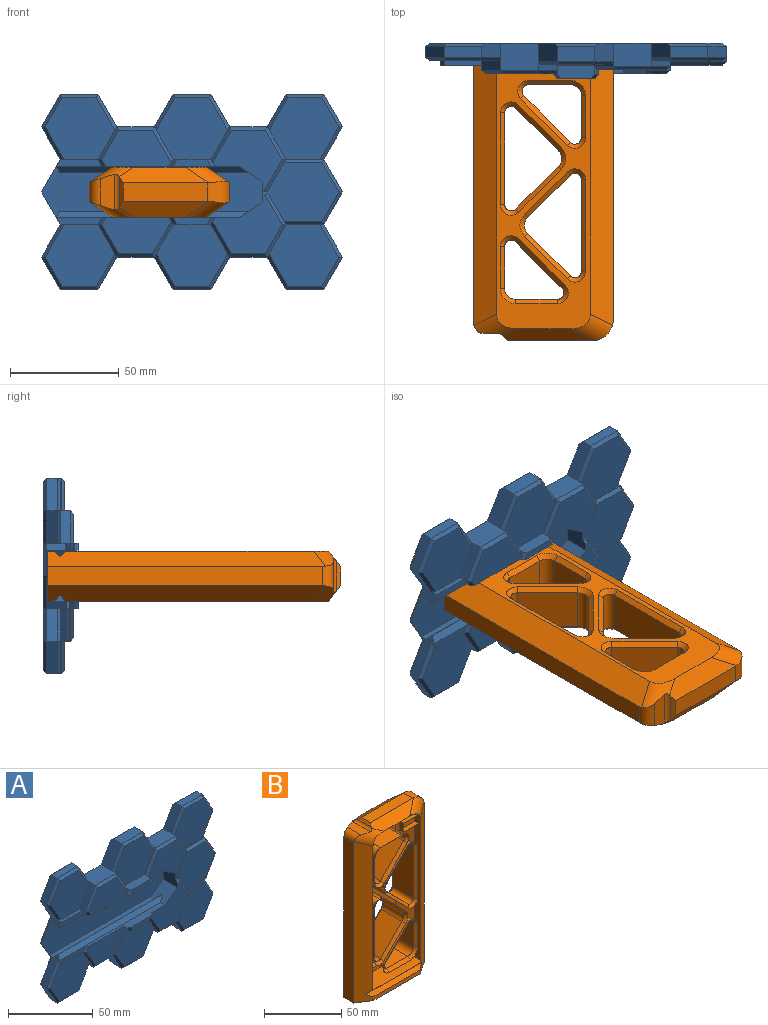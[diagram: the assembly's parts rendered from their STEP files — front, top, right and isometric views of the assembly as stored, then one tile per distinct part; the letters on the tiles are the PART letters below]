
ASSEMBLY  parts=2 mates=1
PART A: 150 faces, bbox 138.6x16x90 mm
  f0: plane 135.1x87mm, normal (0,1,0), area 9642.8mm2, adj f32,f33,f34,f36,f38,f39,f40,f42
  f1: plane 88.32x2.61mm, normal (0,0.71,0.71), area 315.8mm2, adj f2,f4,f65,f149
  f2: plane 88.32x2.61mm, normal (0,-0.71,0.71), area 315.8mm2, adj f1,f65,f66,f77,f149
  f3: plane 101.93x23.5mm, normal (0,-1,0), area 2228.6mm2, adj f4,f5,f6,f8,f9,f17,f30,f65
  f4: plane 84.4x3.14mm, normal (0,0,1), area 265.1mm2, adj f1,f3,f9,f65
  f5: plane 84.4x3.14mm, normal (0,0,-1), area 265.1mm2, adj f3,f8,f17,f147
  f6: plane 12.1x9.2mm, normal (-1,0,0), area 101mm2, adj f3,f8,f10,f12,f65,f70,f145
  f7: plane 63.32x5.74mm, normal (0,0,-1), area 252.4mm2, adj f8,f12,f64,f68,f69,f72,f73,f80
  f8: plane 10.75x10.1mm, normal (-0.55,0,-0.83), area 118.1mm2, adj f3,f5,f6,f7,f12,f80,f147
  f9: plane 15x8.76mm, normal (-0.87,0,-0.5), area 38.3mm2, adj f3,f4,f17,f18,f76,f77,f139,f149
  f10: plane 32.04x27mm, normal (0,-1,0), area 495.5mm2, adj f6,f65,f66,f75,f110,f111,f112,f113
  f11: plane 32.04x16.75mm, normal (0,-1,0), area 415.2mm2, adj f66,f71,f86,f87,f88,f89
  f12: plane 32.04x28.5mm, normal (0,-1,0), area 496.6mm2, adj f6,f7,f8,f69,f70,f82,f83,f84
  f13: plane 17.32x7mm, normal (0,0,1), area 121.2mm2, adj f33,f34,f100,f138
  f14: plane 17.32x5mm, normal (0,0,1), area 86.6mm2, adj f15,f36,f95,f143
  f15: plane 15x8.66mm, normal (-0.87,0,0.5), area 86.6mm2, adj f14,f16,f96,f142
  f16: plane 15x8.66mm, normal (-0.87,0,-0.5), area 86.6mm2, adj f15,f17,f97,f141
  f17: plane 15x8.76mm, normal (-0.87,0,0.5), area 38.3mm2, adj f3,f5,f9,f16,f78,f79,f140,f148
  f18: plane 15x8.66mm, normal (-0.87,0,0.5), area 86.6mm2, adj f9,f19,f137,f146
  f19: plane 15x8.66mm, normal (-0.87,0,-0.5), area 86.6mm2, adj f18,f20,f123,f136
  f20: plane 17.32x5mm, normal (0,0,-1), area 86.6mm2, adj f19,f42,f124,f135
  f21: plane 17.32x7mm, normal (0,0,-1), area 121.2mm2, adj f39,f40,f121,f131
  f22: plane 17.32x5mm, normal (0,0,-1), area 86.6mm2, adj f23,f38,f117,f126
  f23: plane 15x8.66mm, normal (0.87,0,-0.5), area 86.6mm2, adj f22,f24,f118,f127
  f24: plane 15x8.66mm, normal (0.87,0,0.5), area 86.6mm2, adj f23,f25,f119,f128
  f25: plane 15x8.66mm, normal (0.87,0,-0.5), area 121.2mm2, adj f24,f26,f45,f107,f129
  f26: plane 15x8.66mm, normal (0.87,0,0.5), area 121.2mm2, adj f25,f27,f44,f108,f130
  f27: plane 15x8.66mm, normal (0.87,0,-0.5), area 86.6mm2, adj f26,f28,f102,f132
  f28: plane 15x8.66mm, normal (0.87,0,0.5), area 86.6mm2, adj f27,f29,f103,f133
  f29: plane 17.32x5mm, normal (0,0,1), area 86.6mm2, adj f28,f32,f104,f134
  f30: cylinder r=1.8mm len=3.6mm, axis (0,1,0), area 10.2mm2, adj f3,f81
  f31: plane 32.04x28.5mm, normal (0,-1,0), area 678.1mm2, adj f44,f56,f102,f103,f104,f105
  f32: plane 15x8.66mm, normal (-0.87,0,0.5), area 111.3mm2, adj f0,f29,f62,f105,f134
  f33: plane 15x8.66mm, normal (0.87,0,0.5), area 145.9mm2, adj f0,f13,f62,f99,f138
  f34: plane 15x8.66mm, normal (-0.87,0,0.5), area 145.9mm2, adj f0,f13,f63,f101,f138
  f35: plane 32.04x28.5mm, normal (0,-1,0), area 678.1mm2, adj f51,f78,f94,f95,f96,f97
  f36: plane 15x8.66mm, normal (0.87,0,0.5), area 111.3mm2, adj f0,f14,f63,f94,f143
  f37: plane 32.04x28.5mm, normal (0,-1,0), area 678.1mm2, adj f45,f59,f116,f117,f118,f119
  f38: plane 15x8.66mm, normal (-0.87,0,-0.5), area 111.3mm2, adj f0,f22,f61,f116,f126
  f39: plane 15x8.66mm, normal (-0.87,0,-0.5), area 145.9mm2, adj f0,f21,f60,f120,f131
  f40: plane 15x8.66mm, normal (0.87,0,-0.5), area 145.9mm2, adj f0,f21,f61,f122,f131
  f41: plane 32.04x28.5mm, normal (0,-1,0), area 678.1mm2, adj f57,f76,f123,f124,f125,f146
  f42: plane 15x8.66mm, normal (0.87,0,-0.5), area 111.3mm2, adj f0,f20,f60,f125,f135
  f43: plane 32.91x28.5mm, normal (0,-1,0), area 702.8mm2, adj f48,f49,f50,f99,f100,f101
  f44: plane 17.32x2mm, normal (0,0,1), area 10mm2, adj f26,f31,f56,f102,f109
  f45: plane 17.32x2mm, normal (0,0,-1), area 10mm2, adj f25,f37,f59,f106,f119
  f46: plane 32.91x27mm, normal (0,-1,0), area 678.1mm2, adj f55,f58,f106,f107,f108,f109
  f47: plane 32.91x28.5mm, normal (0,-1,0), area 702.8mm2, adj f52,f53,f54,f120,f121,f122
  f48: plane 15x8.66mm, normal (-0.87,0,0.5), area 10mm2, adj f43,f50,f62,f85,f99
  f49: plane 15x8.66mm, normal (0.87,0,0.5), area 44.6mm2, adj f43,f50,f63,f90,f101
  f50: plane 17.32x6mm, normal (0,0,1), area 101.3mm2, adj f43,f48,f49,f69,f72,f73,f98,f144
  f51: plane 15x8.66mm, normal (-0.87,0,0.5), area 79.2mm2, adj f35,f63,f64,f78,f92,f94
  f52: plane 15x8.66mm, normal (-0.87,0,-0.5), area 44.6mm2, adj f47,f53,f61,f110,f122
  f53: plane 17.32x6mm, normal (0,0,-1), area 101.3mm2, adj f47,f52,f54,f71,f74,f75,f114,f115
  f54: plane 15x8.66mm, normal (0.87,0,-0.5), area 10mm2, adj f47,f53,f60,f86,f120
  f55: plane 15x8.66mm, normal (0.87,0,-0.5), area 10mm2, adj f46,f56,f58,f82,f109
  f56: plane 15x8.66mm, normal (0.87,0,0.5), area 44.6mm2, adj f31,f44,f55,f62,f83,f105
  f57: plane 15x8.66mm, normal (-0.87,0,-0.5), area 44.6mm2, adj f41,f60,f67,f76,f88,f125
  f58: plane 15x8.66mm, normal (0.87,0,0.5), area 44.6mm2, adj f46,f55,f59,f70,f106,f113
  f59: plane 15x8.66mm, normal (0.87,0,-0.5), area 79.2mm2, adj f37,f45,f58,f61,f112,f116
  f60: plane 17.32x10.5mm, normal (0,0,-1), area 181.9mm2, adj f0,f39,f42,f54,f57,f87
  f61: plane 17.32x12.5mm, normal (0,0,-1), area 216.5mm2, adj f0,f38,f40,f52,f59,f111
  f62: plane 17.32x10.5mm, normal (0,0,1), area 181.9mm2, adj f0,f32,f33,f48,f56,f84
  f63: plane 17.32x12.5mm, normal (0,0,1), area 216.5mm2, adj f0,f34,f36,f49,f51,f91
  f64: plane 3.25x2.24mm, normal (-0.87,0,-0.5), area 8.4mm2, adj f7,f51,f79,f93
  f65: plane 12.1x10.75mm, normal (-0.55,0,0.83), area 143.9mm2, adj f1,f2,f3,f4,f6,f10,f66
  f66: plane 63.32x5.74mm, normal (0,0,1), area 213.4mm2, adj f2,f10,f11,f65,f67,f71,f74,f75
  f67: plane 3.25x1.88mm, normal (-0.87,0,0.5), area 0.9mm2, adj f57,f66,f77,f89
  f68: plane 32.04x16.75mm, normal (0,-1,0), area 415.2mm2, adj f7,f73,f90,f91,f92,f93
  f69: plane 4x3.25mm, normal (0.87,0,0.5), area 10.7mm2, adj f7,f12,f50,f85,f144
  f70: plane 2x1.99mm, normal (0,0,1), area 2.3mm2, adj f6,f12,f58,f82,f145
  f71: plane 4x3.25mm, normal (-0.87,0,-0.5), area 10.7mm2, adj f11,f53,f66,f86,f114
  f72: plane 17.61x3.25mm, normal (0,-1,0), area 51.1mm2, adj f7,f50,f98,f144
  f73: plane 3.25x2mm, normal (-0.87,0,0.5), area 3.2mm2, adj f7,f50,f68,f90,f98
  f74: plane 17.61x3.25mm, normal (0,-1,0), area 51.1mm2, adj f53,f66,f114,f115
  f75: plane 3.25x2mm, normal (0.87,0,-0.5), area 3.2mm2, adj f10,f53,f66,f110,f115
  f76: plane 17.32x3.76mm, normal (0,0,-1), area 40.4mm2, adj f9,f41,f57,f77,f146
  f77: plane 21.07x3.25mm, normal (0,-1,0), area 62.4mm2, adj f2,f9,f67,f76
  f78: plane 17.32x3.76mm, normal (0,0,1), area 40.4mm2, adj f17,f35,f51,f79,f97
  f79: plane 21.07x3.25mm, normal (0,-1,0), area 62.4mm2, adj f17,f64,f78,f80
  f80: plane 88.32x2.61mm, normal (0,-0.71,-0.71), area 315.8mm2, adj f7,f8,f79,f147,f148
  f81: cone r=2.8mm half-angle=45deg, axis (0,1,0), area 20.4mm2, adj f0,f30
  f82: plane 15x10.39mm, normal (0.61,-0.71,-0.35), area 36.7mm2, adj f12,f55,f70,f83
  f83: plane 15x9.53mm, normal (0.61,-0.71,0.35), area 34.9mm2, adj f12,f56,f82,f84
  f84: plane 17.32x1.5mm, normal (0,-0.71,0.71), area 34.9mm2, adj f12,f62,f83,f85
  f85: plane 16.5x9.53mm, normal (-0.61,-0.71,0.35), area 36.7mm2, adj f12,f48,f69,f84
  f86: plane 16.5x9.53mm, normal (0.61,-0.71,-0.35), area 36.7mm2, adj f11,f54,f71,f87
  f87: plane 17.32x1.5mm, normal (0,-0.71,-0.71), area 34.9mm2, adj f11,f60,f86,f88
  f88: plane 15x9.53mm, normal (-0.61,-0.71,-0.35), area 34.9mm2, adj f11,f57,f87,f89
  f89: plane 3.61x3.25mm, normal (-0.61,-0.71,0.35), area 8mm2, adj f11,f66,f67,f88
  f90: plane 16.5x9.53mm, normal (0.61,-0.71,0.35), area 36.7mm2, adj f49,f68,f73,f91
  f91: plane 17.32x1.5mm, normal (0,-0.71,0.71), area 34.9mm2, adj f63,f68,f90,f92
  f92: plane 15x9.53mm, normal (-0.61,-0.71,0.35), area 34.9mm2, adj f51,f68,f91,f93
  f93: plane 3.61x3.25mm, normal (-0.61,-0.71,-0.35), area 8mm2, adj f7,f64,f68,f92
  f94: plane 16.5x9.53mm, normal (0.61,-0.71,0.35), area 36.7mm2, adj f35,f36,f51,f95
  f95: plane 17.32x1.5mm, normal (0,-0.71,0.71), area 34.9mm2, adj f14,f35,f94,f96
  f96: plane 15x9.53mm, normal (-0.61,-0.71,0.35), area 34.9mm2, adj f15,f35,f95,f97
  f97: plane 15x10.39mm, normal (-0.61,-0.71,-0.35), area 36.7mm2, adj f16,f35,f78,f96
  f98: plane 3.61x3.25mm, normal (-0.61,-0.71,0.35), area 8mm2, adj f7,f50,f72,f73
  f99: plane 16.5x9.53mm, normal (0.61,-0.71,0.35), area 36.7mm2, adj f33,f43,f48,f100
  f100: plane 17.32x1.5mm, normal (0,-0.71,0.71), area 34.9mm2, adj f13,f43,f99,f101
  f101: plane 16.5x9.53mm, normal (-0.61,-0.71,0.35), area 36.7mm2, adj f34,f43,f49,f100
  f102: plane 15x10.39mm, normal (0.61,-0.71,-0.35), area 36.7mm2, adj f27,f31,f44,f103
  f103: plane 15x9.53mm, normal (0.61,-0.71,0.35), area 34.9mm2, adj f28,f31,f102,f104
  f104: plane 17.32x1.5mm, normal (0,-0.71,0.71), area 34.9mm2, adj f29,f31,f103,f105
  f105: plane 16.5x9.53mm, normal (-0.61,-0.71,0.35), area 36.7mm2, adj f31,f32,f56,f104
  f106: plane 18.19x1.5mm, normal (0,-0.71,-0.71), area 36.7mm2, adj f45,f46,f58,f107
  f107: plane 15x9.53mm, normal (0.61,-0.71,-0.35), area 34.9mm2, adj f25,f46,f106,f108
  f108: plane 15x9.53mm, normal (0.61,-0.71,0.35), area 34.9mm2, adj f26,f46,f107,f109
  f109: plane 18.19x1.5mm, normal (0,-0.71,0.71), area 36.7mm2, adj f44,f46,f55,f108
  f110: plane 16.5x9.53mm, normal (-0.61,-0.71,-0.35), area 36.7mm2, adj f10,f52,f75,f111
  f111: plane 17.32x1.5mm, normal (0,-0.71,-0.71), area 34.9mm2, adj f10,f61,f110,f112
  f112: plane 15x9.53mm, normal (0.61,-0.71,-0.35), area 34.9mm2, adj f10,f59,f111,f113
  f113: plane 15x9.53mm, normal (0.61,-0.71,0.35), area 34.9mm2, adj f10,f58,f112,f145
  f114: plane 3.61x3.25mm, normal (-0.61,-0.71,-0.35), area 8mm2, adj f53,f66,f71,f74
  f115: plane 3.61x3.25mm, normal (0.61,-0.71,-0.35), area 8mm2, adj f53,f66,f74,f75
  f116: plane 16.5x9.53mm, normal (-0.61,-0.71,-0.35), area 36.7mm2, adj f37,f38,f59,f117
  f117: plane 17.32x1.5mm, normal (0,-0.71,-0.71), area 34.9mm2, adj f22,f37,f116,f118
  f118: plane 15x9.53mm, normal (0.61,-0.71,-0.35), area 34.9mm2, adj f23,f37,f117,f119
  f119: plane 15x10.39mm, normal (0.61,-0.71,0.35), area 36.7mm2, adj f24,f37,f45,f118
  f120: plane 16.5x9.53mm, normal (-0.61,-0.71,-0.35), area 36.7mm2, adj f39,f47,f54,f121
  f121: plane 17.32x1.5mm, normal (0,-0.71,-0.71), area 34.9mm2, adj f21,f47,f120,f122
  f122: plane 16.5x9.53mm, normal (0.61,-0.71,-0.35), area 36.7mm2, adj f40,f47,f52,f121
  f123: plane 15x9.53mm, normal (-0.61,-0.71,-0.35), area 34.9mm2, adj f19,f41,f124,f146
  f124: plane 17.32x1.5mm, normal (0,-0.71,-0.71), area 34.9mm2, adj f20,f41,f123,f125
  f125: plane 16.5x9.53mm, normal (0.61,-0.71,-0.35), area 36.7mm2, adj f41,f42,f57,f124
  f126: plane 18.19x1.5mm, normal (0,0.71,-0.71), area 36.7mm2, adj f0,f22,f38,f127
  f127: plane 15x9.53mm, normal (0.61,0.71,-0.35), area 34.9mm2, adj f0,f23,f126,f128
  f128: plane 15x10.39mm, normal (0.61,0.71,0.35), area 36.7mm2, adj f0,f24,f127,f129
  f129: plane 15x10.39mm, normal (0.61,0.71,-0.35), area 36.7mm2, adj f0,f25,f128,f130
  f130: plane 15x10.39mm, normal (0.61,0.71,0.35), area 36.7mm2, adj f0,f26,f129,f132
  f131: plane 19.05x1.5mm, normal (0,0.71,-0.71), area 38.6mm2, adj f0,f21,f39,f40
  f132: plane 15x10.39mm, normal (0.61,0.71,-0.35), area 36.7mm2, adj f0,f27,f130,f133
  f133: plane 15x9.53mm, normal (0.61,0.71,0.35), area 34.9mm2, adj f0,f28,f132,f134
  f134: plane 18.19x1.5mm, normal (0,0.71,0.71), area 36.7mm2, adj f0,f29,f32,f133
  f135: plane 18.19x1.5mm, normal (0,0.71,-0.71), area 36.7mm2, adj f0,f20,f42,f136
  f136: plane 15x9.53mm, normal (-0.61,0.71,-0.35), area 34.9mm2, adj f0,f19,f135,f137
  f137: plane 15x10.39mm, normal (-0.61,0.71,0.35), area 36.7mm2, adj f0,f18,f136,f139
  f138: plane 19.05x1.5mm, normal (0,0.71,0.71), area 38.6mm2, adj f0,f13,f33,f34
  f139: plane 15x10.39mm, normal (-0.61,0.71,-0.35), area 36.7mm2, adj f0,f9,f137,f140
  f140: plane 15x10.39mm, normal (-0.61,0.71,0.35), area 36.7mm2, adj f0,f17,f139,f141
  f141: plane 15x10.39mm, normal (-0.61,0.71,-0.35), area 36.7mm2, adj f0,f16,f140,f142
  f142: plane 15x9.53mm, normal (-0.61,0.71,0.35), area 34.9mm2, adj f0,f15,f141,f143
  f143: plane 18.19x1.5mm, normal (0,0.71,0.71), area 36.7mm2, adj f0,f14,f36,f142
  f144: plane 3.61x3.25mm, normal (0.61,-0.71,0.35), area 8mm2, adj f7,f50,f69,f72
  f145: plane 1.99x1.5mm, normal (0,-0.71,0.71), area 3.3mm2, adj f6,f10,f70,f113
  f146: plane 15x10.39mm, normal (-0.61,-0.71,0.35), area 36.7mm2, adj f18,f41,f76,f123
  f147: plane 88.32x2.61mm, normal (0,0.71,-0.71), area 315.8mm2, adj f5,f8,f80,f148
  f148: plane 5.22x2.61mm, normal (-0.87,0,-0.5), area 7.9mm2, adj f17,f80,f147
  f149: plane 5.22x2.61mm, normal (-0.87,0,0.5), area 7.9mm2, adj f1,f2,f9
PART B: 106 faces, bbox 64.6x28.6x136.7 mm
  f0: plane 121.2x43.15mm, normal (0,-1,0), area 1725.4mm2, adj f7,f8,f16,f18,f19,f20,f21,f27
  f1: plane 121.2x43.15mm, normal (0,1,0), area 1823.4mm2, adj f14,f23,f24,f25,f31,f32,f58,f59
  f2: cylinder r=10mm len=10.08mm, axis (0,1,0), area 139.6mm2, adj f3,f8,f11,f23,f25,f27,f30,f31
  f3: plane 39x8.37mm, normal (0,0,1), area 326.3mm2, adj f2,f5,f26,f28
  f4: plane 16.28x6.7mm, normal (0,0,1), area 96.8mm2, adj f6,f29,f32,f33
  f5: plane 13.29x1.86mm, normal (-0.78,0,0.62), area 25.8mm2, adj f3,f6,f25,f26,f27,f28
  f6: cylinder r=3.13mm len=16.32mm, axis (0,1,0), area 44.8mm2, adj f4,f5,f25,f27,f29,f32
  f7: plane 128.12x10.74mm, normal (-0.55,-0.83,0), area 1595.8mm2, adj f0,f9,f10,f13,f16,f17,f29,f33
  f8: plane 128.03x10.74mm, normal (0.55,-0.83,0), area 1595.5mm2, adj f0,f2,f9,f11,f13,f16,f17,f30
  f9: plane 64.5x23mm, normal (0,0,-1), area 1332mm2, adj f7,f8,f10,f11,f12,f13,f23,f24
  f10: plane 126.69x8.8mm, normal (-1,0,0), area 1115.3mm2, adj f7,f9,f24,f33
  f11: plane 125.91x8.8mm, normal (1,0,0), area 1108.5mm2, adj f2,f8,f9,f23
  f12: plane 43.15x3.03mm, normal (0,1,0), area 130.5mm2, adj f9,f15,f23,f24
  f13: plane 43.15x3.03mm, normal (0,-1,0), area 130.5mm2, adj f7,f8,f9,f17
  f14: plane 51.12x2.65mm, normal (0,0.71,-0.71), area 176.7mm2, adj f1,f15,f23,f24
  f15: plane 51.12x2.65mm, normal (0,0.71,0.71), area 176.7mm2, adj f12,f14,f23,f24
  f16: plane 51.12x2.65mm, normal (0,-0.71,-0.71), area 176.7mm2, adj f0,f7,f8,f17
  f17: plane 51.12x2.65mm, normal (0,-0.71,0.71), area 176.7mm2, adj f7,f8,f13,f16
  f18: plane 14x3.5mm, normal (0,0,-1), area 49mm2, adj f0,f19,f21,f22
  f19: plane 7x3.5mm, normal (1,0,0), area 24.5mm2, adj f0,f18,f20,f22
  f20: plane 14x3.5mm, normal (0,0,1), area 49mm2, adj f0,f19,f21,f22
  f21: plane 7x3.5mm, normal (-1,0,0), area 24.5mm2, adj f0,f18,f20,f22
  f22: plane 14x7mm, normal (0,-1,0), area 98mm2, adj f18,f19,f20,f21
  f23: plane 128.03x10.74mm, normal (0.55,0.83,0), area 1595.5mm2, adj f1,f2,f9,f11,f12,f14,f15,f31
  f24: plane 128.12x10.74mm, normal (-0.55,0.83,0), area 1595.8mm2, adj f1,f9,f10,f12,f14,f15,f32,f33
  f25: plane 41.32x7.33mm, normal (0,0.6,0.8), area 307mm2, adj f1,f2,f5,f6,f26,f31,f32
  f26: plane 39.01x0.01mm, normal (0,1,0), area 0.2mm2, adj f3,f5,f25
  f27: plane 41.32x7.33mm, normal (0,-0.6,0.8), area 307mm2, adj f0,f2,f5,f6,f28,f29,f30
  f28: plane 39.01x0.01mm, normal (0,-1,0), area 0.2mm2, adj f3,f5,f27
  f29: cylinder r=10.73mm len=20.17mm, axis (-0.77,0.51,0.38), area 113.3mm2, adj f0,f4,f6,f7,f27,f33
  f30: cylinder r=10.73mm len=19.97mm, axis (-0.77,-0.51,-0.38), area 147.5mm2, adj f0,f2,f8,f27
  f31: cylinder r=10.73mm len=19.97mm, axis (0.77,-0.51,0.38), area 147.5mm2, adj f1,f2,f23,f25
  f32: cylinder r=10.73mm len=20.17mm, axis (0.77,0.51,-0.38), area 113.3mm2, adj f1,f4,f6,f24,f25,f33
  f33: cylinder r=5mm len=12.2mm, axis (0,1,0), area 79.8mm2, adj f4,f7,f10,f24,f29,f32
  f34: plane 19.31x19mm, normal (0,0,1), area 366.8mm2, adj f35,f39,f61,f91
  f35: cylinder r=5mm len=19mm, axis (0,1,0), area 149.2mm2, adj f34,f36,f63,f89
  f36: plane 19.31x19mm, normal (-1,0,0), area 366.8mm2, adj f35,f37,f62,f88
  f37: cylinder r=3mm len=19mm, axis (0,1,0), area 134.3mm2, adj f36,f38,f60,f90
  f38: plane 21.31x21.31mm, normal (0.71,0,-0.71), area 572.5mm2, adj f37,f39,f58,f92
  f39: cylinder r=3mm len=19mm, axis (0,1,0), area 134.3mm2, adj f34,f38,f59,f93
  f40: plane 19.31x19mm, normal (1,0,0), area 366.8mm2, adj f41,f45,f76,f103
  f41: cylinder r=3mm len=19mm, axis (0,1,0), area 134.3mm2, adj f40,f42,f77,f101
  f42: plane 21.31x21.31mm, normal (-0.71,0,0.71), area 572.5mm2, adj f41,f43,f79,f100
  f43: cylinder r=3mm len=19mm, axis (0,1,0), area 134.3mm2, adj f42,f44,f81,f102
  f44: plane 19.31x19mm, normal (0,0,-1), area 366.8mm2, adj f43,f45,f80,f104
  f45: cylinder r=5mm len=19mm, axis (0,1,0), area 149.2mm2, adj f40,f44,f78,f105
  f46: plane 19.67x19.67mm, normal (-0.71,0,0.71), area 528.6mm2, adj f47,f51,f67,f85
  f47: cylinder r=5mm len=19mm, axis (0,1,0), area 149.2mm2, adj f46,f48,f69,f83
  f48: plane 19.67x19.67mm, normal (-0.71,0,-0.71), area 528.6mm2, adj f47,f49,f68,f82
  f49: cylinder r=3mm len=19mm, axis (0,1,0), area 134.3mm2, adj f48,f50,f66,f84
  f50: plane 42.18x19mm, normal (1,0,0), area 801.4mm2, adj f49,f51,f64,f86
  f51: cylinder r=3mm len=19mm, axis (0,1,0), area 134.3mm2, adj f46,f50,f65,f87
  f52: plane 42.18x19mm, normal (-1,0,0), area 801.4mm2, adj f53,f57,f74,f94
  f53: cylinder r=3mm len=19mm, axis (0,1,0), area 134.3mm2, adj f52,f54,f72,f96
  f54: plane 19.67x19.67mm, normal (0.71,0,-0.71), area 528.6mm2, adj f53,f55,f70,f98
  f55: cylinder r=5mm len=19mm, axis (0,1,0), area 149.2mm2, adj f54,f56,f71,f99
  f56: plane 19.67x19.67mm, normal (0.71,0,0.71), area 528.6mm2, adj f55,f57,f73,f97
  f57: cylinder r=3mm len=19mm, axis (0,1,0), area 134.3mm2, adj f52,f56,f75,f95
  f58: plane 22.72x22.72mm, normal (0.5,0.71,-0.5), area 85.2mm2, adj f1,f38,f59,f60
  f59: cone r=5mm half-angle=45deg, axis (0,1,0), area 26.7mm2, adj f1,f39,f58,f61
  f60: cone r=5mm half-angle=45deg, axis (0,1,0), area 26.7mm2, adj f1,f37,f58,f62
  f61: plane 19.31x2mm, normal (0,0.71,0.71), area 54.6mm2, adj f1,f34,f59,f63
  f62: plane 19.31x2mm, normal (-0.71,0.71,0), area 54.6mm2, adj f1,f36,f60,f63
  f63: cone r=7mm half-angle=45deg, axis (0,1,0), area 26.7mm2, adj f1,f35,f61,f62
  f64: plane 42.18x2mm, normal (0.71,0.71,0), area 119.3mm2, adj f1,f50,f65,f66
  f65: cone r=5mm half-angle=45deg, axis (0,1,0), area 26.7mm2, adj f1,f51,f64,f67
  f66: cone r=5mm half-angle=45deg, axis (0,1,0), area 26.7mm2, adj f1,f49,f64,f68
  f67: plane 21.09x21.09mm, normal (-0.5,0.71,0.5), area 78.7mm2, adj f1,f46,f65,f69
  f68: plane 21.09x21.09mm, normal (-0.5,0.71,-0.5), area 78.7mm2, adj f1,f48,f66,f69
  f69: cone r=7mm half-angle=45deg, axis (0,1,0), area 26.7mm2, adj f1,f47,f67,f68
  f70: plane 21.09x21.09mm, normal (0.5,0.71,-0.5), area 78.7mm2, adj f1,f54,f71,f72
  f71: cone r=7mm half-angle=45deg, axis (0,1,0), area 26.7mm2, adj f1,f55,f70,f73
  f72: cone r=5mm half-angle=45deg, axis (0,1,0), area 26.7mm2, adj f1,f53,f70,f74
  f73: plane 21.09x21.09mm, normal (0.5,0.71,0.5), area 78.7mm2, adj f1,f56,f71,f75
  f74: plane 42.18x2mm, normal (-0.71,0.71,0), area 119.3mm2, adj f1,f52,f72,f75
  f75: cone r=5mm half-angle=45deg, axis (0,1,0), area 26.7mm2, adj f1,f57,f73,f74
  f76: plane 19.31x2mm, normal (0.71,0.71,0), area 54.6mm2, adj f1,f40,f77,f78
  f77: cone r=5mm half-angle=45deg, axis (0,1,0), area 26.7mm2, adj f1,f41,f76,f79
  f78: cone r=7mm half-angle=45deg, axis (0,1,0), area 26.7mm2, adj f1,f45,f76,f80
  f79: plane 22.72x22.72mm, normal (-0.5,0.71,0.5), area 85.2mm2, adj f1,f42,f77,f81
  f80: plane 19.31x2mm, normal (0,0.71,-0.71), area 54.6mm2, adj f1,f44,f78,f81
  f81: cone r=5mm half-angle=45deg, axis (0,1,0), area 26.7mm2, adj f1,f43,f79,f80
  f82: plane 21.09x21.09mm, normal (-0.5,-0.71,-0.5), area 78.7mm2, adj f0,f48,f83,f84
  f83: cone r=7mm half-angle=45deg, axis (0,-1,0), area 26.7mm2, adj f0,f47,f82,f85
  f84: cone r=5mm half-angle=45deg, axis (0,-1,0), area 26.7mm2, adj f0,f49,f82,f86
  f85: plane 21.09x21.09mm, normal (-0.5,-0.71,0.5), area 78.7mm2, adj f0,f46,f83,f87
  f86: plane 42.18x2mm, normal (0.71,-0.71,0), area 119.3mm2, adj f0,f50,f84,f87
  f87: cone r=5mm half-angle=45deg, axis (0,-1,0), area 26.7mm2, adj f0,f51,f85,f86
  f88: plane 19.31x2mm, normal (-0.71,-0.71,0), area 54.6mm2, adj f0,f36,f89,f90
  f89: cone r=7mm half-angle=45deg, axis (0,-1,0), area 26.7mm2, adj f0,f35,f88,f91
  f90: cone r=5mm half-angle=45deg, axis (0,-1,0), area 26.7mm2, adj f0,f37,f88,f92
  f91: plane 19.31x2mm, normal (0,-0.71,0.71), area 54.6mm2, adj f0,f34,f89,f93
  f92: plane 22.72x22.72mm, normal (0.5,-0.71,-0.5), area 85.2mm2, adj f0,f38,f90,f93
  f93: cone r=5mm half-angle=45deg, axis (0,-1,0), area 26.7mm2, adj f0,f39,f91,f92
  f94: plane 42.18x2mm, normal (-0.71,-0.71,0), area 119.3mm2, adj f0,f52,f95,f96
  f95: cone r=5mm half-angle=45deg, axis (0,-1,0), area 26.7mm2, adj f0,f57,f94,f97
  f96: cone r=5mm half-angle=45deg, axis (0,-1,0), area 26.7mm2, adj f0,f53,f94,f98
  f97: plane 21.09x21.09mm, normal (0.5,-0.71,0.5), area 78.7mm2, adj f0,f56,f95,f99
  f98: plane 21.09x21.09mm, normal (0.5,-0.71,-0.5), area 78.7mm2, adj f0,f54,f96,f99
  f99: cone r=7mm half-angle=45deg, axis (0,-1,0), area 26.7mm2, adj f0,f55,f97,f98
  f100: plane 22.72x22.72mm, normal (-0.5,-0.71,0.5), area 85.2mm2, adj f0,f42,f101,f102
  f101: cone r=5mm half-angle=45deg, axis (0,-1,0), area 26.7mm2, adj f0,f41,f100,f103
  f102: cone r=5mm half-angle=45deg, axis (0,-1,0), area 26.7mm2, adj f0,f43,f100,f104
  f103: plane 19.31x2mm, normal (0.71,-0.71,0), area 54.6mm2, adj f0,f40,f101,f105
  f104: plane 19.31x2mm, normal (0,-0.71,-0.71), area 54.6mm2, adj f0,f44,f102,f105
  f105: cone r=7mm half-angle=45deg, axis (0,-1,0), area 26.7mm2, adj f0,f45,f103,f104
PLACE A t=(15.06,8.89,-0.04)mm
PLACE B rot(axis=(1,0,0),90deg) t=(36.64,-99.04,11.43)mm
MATE planar B.f9 <-> A.f30  axis (0,1,0) through (0.06,6.99,-0.07)mm
